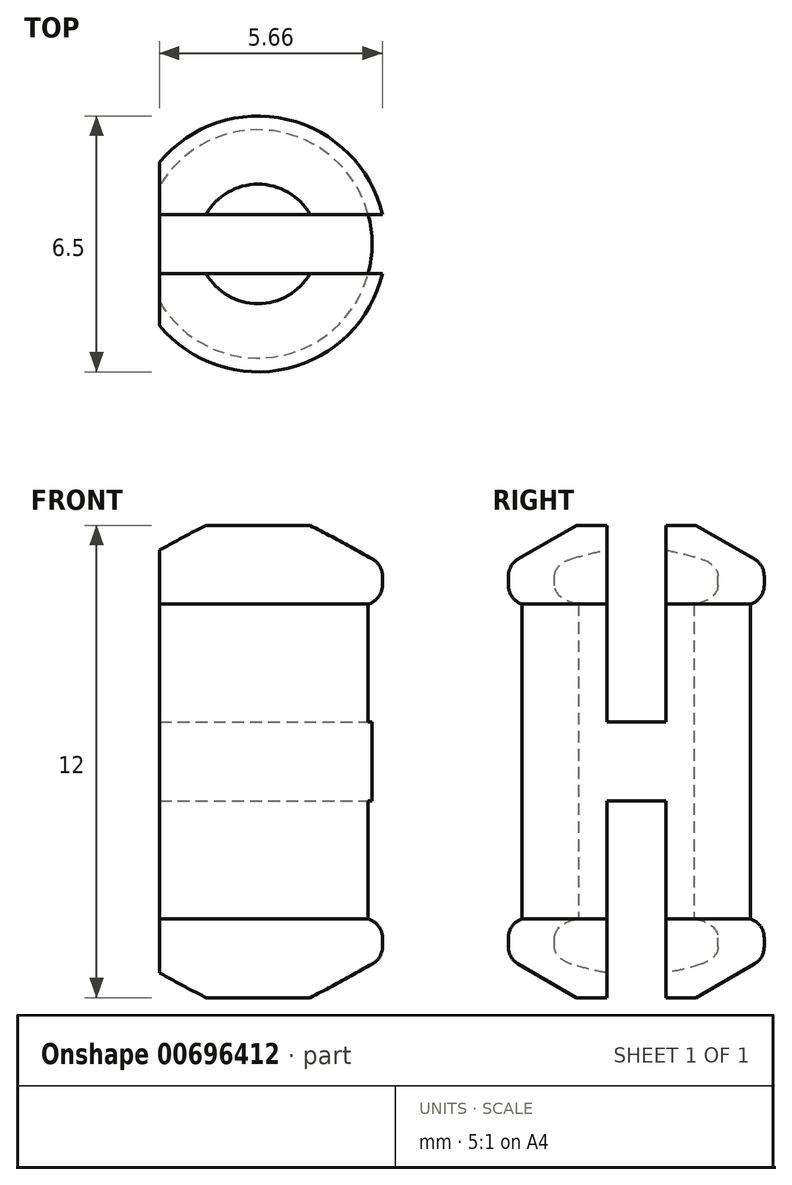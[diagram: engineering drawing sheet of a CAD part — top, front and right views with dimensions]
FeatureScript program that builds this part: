
annotation { "Feature Type Name" : "Feature", "Feature Type Description" : "" }
export const myFeature = defineFeature(function(context is Context, id is Id, definition is map)
    precondition{}
    {
        {
            var Q0;
            Q0=qCreatedBy(makeId("Top.planeOp"),FACE);
            var sketch = newSketch(context, id + "F0", { "sketchPlane" : qUnion([Q0])});
            skCircle(sketch, "E0", {"center": v(0, 0) * mm, "radius": 3.25 * mm});
            skSolve(sketch);
        }
        {
            var Q0;
            Q0=qSketchRegion(id+"F0",true);
            extrude(context, id + "F1", {"entities" : qUnion([Q0]), "depth" : 2 * mm, "offsetDistance" : 25 * mm});
        }
        {
            var Q0;
            Q0=makeQuery(id+"F1.opExtrude","CAP_FACE",FACE,{"disambiguationData":[OSD([sQuery(id+"F0.wireOp",EDGE,"E0")])],"isStart":false});
            var sketch = newSketch(context, id + "F2", { "sketchPlane" : qUnion([Q0])});
            skCircle(sketch, "E1", {"center": v(0, 0) * mm, "radius": 2.9 * mm});
            skSolve(sketch);
        }
        {
            var Q0;
            Q0=qSketchRegion(id+"F2",true);
            extrude(context, id + "F3", {"entities" : qUnion([Q0]), "operationType" : NewBodyOperationType.ADD, "depth" : 8 * mm, "offsetDistance" : 25 * mm});
        }
        {
            var Q0;
            Q0=makeQuery(id+"F3.opExtrude","CAP_FACE",FACE,{"disambiguationData":[OSD([sQuery(id+"F2.wireOp",EDGE,"E1")])],"isStart":false});
            var sketch = newSketch(context, id + "F4", { "sketchPlane" : qUnion([Q0])});
            skCircle(sketch, "E2", {"center": v(0, 0) * mm, "radius": 3.25 * mm});
            skSolve(sketch);
        }
        {
            var Q0;
            Q0=qSketchRegion(id+"F4",true);
            extrude(context, id + "F5", {"entities" : qUnion([Q0]), "operationType" : NewBodyOperationType.ADD, "depth" : 2 * mm, "offsetDistance" : 25 * mm});
        }
        {
            var Q0;
            Q0=makeQuery(id+"F1.opExtrude","CAP_EDGE",EDGE,{"disambiguationData":[OSD([sQuery(id+"F0.wireOp",EDGE,"E0")])],"isStart":false});
            var Q1;
            Q1=makeQuery(id+"F5.opExtrude","CAP_EDGE",EDGE,{"disambiguationData":[OSD([sQuery(id+"F4.wireOp",EDGE,"E2")])],"isStart":true});
            fillet(context, id + "F6", {"entities" : qUnion([Q0, Q1]), "radius" : 0.5 * mm, "tangentPropagation" : true, "allowEdgeOverflow" : false});
        }
        {
            var Q0;
            Q0=makeQuery(id+"F1.opExtrude","CAP_FACE",FACE,{"disambiguationData":[OSD([sQuery(id+"F0.wireOp",EDGE,"E0")])],"isStart":true});
            var sketch = newSketch(context, id + "F7", { "sketchPlane" : qUnion([Q0])});
            skLineSegment(sketch, "E3", {"start": v(-3.16, -0.75) * mm, "end": v(3.16, -0.75) * mm});
            skLineSegment(sketch, "E4", {"start": v(3.16, 0.75) * mm, "end": v(-3.16, 0.75) * mm});
            skArc(sketch, "E5", {"start": v(-3.16, 0.75) * mm, "mid": v(-3.25, 0) * mm, "end": v(-3.16, -0.75) * mm});
            skArc(sketch, "E6", {"start": v(3.16, -0.75) * mm, "mid": v(3.25, 0) * mm, "end": v(3.16, 0.75) * mm});
            skSolve(sketch);
        }
        {
            var Q0;
            Q0=qSketchRegion(id+"F7",true);
            extrude(context, id + "F8", {"entities" : qUnion([Q0]), "operationType" : NewBodyOperationType.REMOVE, "oppositeDirection" : true, "depth" : 5 * mm, "offsetDistance" : 25 * mm});
        }
        {
            var Q0;
            Q0=makeQuery(id+"F5.opExtrude","CAP_FACE",FACE,{"disambiguationData":[OSD([sQuery(id+"F4.wireOp",EDGE,"E2")])],"isStart":false});
            var sketch = newSketch(context, id + "F9", { "sketchPlane" : qUnion([Q0])});
            skLineSegment(sketch, "E7", {"start": v(-3.16, -0.75) * mm, "end": v(3.16, -0.75) * mm});
            skLineSegment(sketch, "E8", {"start": v(3.16, 0.75) * mm, "end": v(-3.16, 0.75) * mm});
            skArc(sketch, "E9", {"start": v(3.16, -0.75) * mm, "mid": v(3.25, 0) * mm, "end": v(3.16, 0.75) * mm});
            skArc(sketch, "E10", {"start": v(-3.16, 0.75) * mm, "mid": v(-3.25, 0) * mm, "end": v(-3.16, -0.75) * mm});
            skSolve(sketch);
        }
        {
            var Q0;
            Q0=qSketchRegion(id+"F9",true);
            extrude(context, id + "F10", {"entities" : qUnion([Q0]), "operationType" : NewBodyOperationType.REMOVE, "oppositeDirection" : true, "depth" : 5 * mm, "offsetDistance" : 25 * mm});
        }
        {
            var Q0;
            {var subQ0=sQuery(id+"F0.wireOp",EDGE,"E0");Q0=makeQuery(id+"F8.boolean.opBoolean","SPLIT",EDGE,{"disambiguationData":[TD([makeQuery(id+"F8.opExtrude","SWEPT_FACE",FACE,{"disambiguationData":[OSD([sQuery(id+"F7.wireOp",EDGE,"E3")])]})])],"derivedFrom":makeQuery(id+"F1.opExtrude","CAP_EDGE",EDGE,{"disambiguationData":[OSD([subQ0])],"isStart":true})});}
            var Q1;
            {var subQ0=sQuery(id+"F0.wireOp",EDGE,"E0");Q1=makeQuery(id+"F8.boolean.opBoolean","SPLIT",EDGE,{"disambiguationData":[TD([makeQuery(id+"F8.opExtrude","SWEPT_FACE",FACE,{"disambiguationData":[OSD([sQuery(id+"F7.wireOp",EDGE,"E4")])]})])],"derivedFrom":makeQuery(id+"F1.opExtrude","CAP_EDGE",EDGE,{"disambiguationData":[OSD([subQ0])],"isStart":true})});}
            chamfer(context, id + "F11", {"entities" : qUnion([Q0, Q1]), "chamferType" : ChamferType.OFFSET_ANGLE, "width" : 1 * mm, "oppositeDirection" : false, "angle" : 60 * degree, "tangentPropagation" : true});
        }
        {
            var Q0;
            {var subQ0=sQuery(id+"F4.wireOp",EDGE,"E2");Q0=makeQuery(id+"F10.boolean.opBoolean","SPLIT",EDGE,{"disambiguationData":[TD([makeQuery(id+"F10.opExtrude","SWEPT_FACE",FACE,{"disambiguationData":[OSD([sQuery(id+"F9.wireOp",EDGE,"E7")])]})])],"derivedFrom":makeQuery(id+"F5.opExtrude","CAP_EDGE",EDGE,{"disambiguationData":[OSD([subQ0])],"isStart":false})});}
            var Q1;
            {var subQ0=sQuery(id+"F4.wireOp",EDGE,"E2");Q1=makeQuery(id+"F10.boolean.opBoolean","SPLIT",EDGE,{"disambiguationData":[TD([makeQuery(id+"F10.opExtrude","SWEPT_FACE",FACE,{"disambiguationData":[OSD([sQuery(id+"F9.wireOp",EDGE,"E8")])]})])],"derivedFrom":makeQuery(id+"F5.opExtrude","CAP_EDGE",EDGE,{"disambiguationData":[OSD([subQ0])],"isStart":false})});}
            chamfer(context, id + "F12", {"entities" : qUnion([Q0, Q1]), "chamferType" : ChamferType.OFFSET_ANGLE, "width" : 1 * mm, "oppositeDirection" : true, "angle" : 60 * degree, "tangentPropagation" : true});
        }
        {
            var Q0;
            {var subQ0=sQuery(id+"F4.wireOp",EDGE,"E2");var subQ2=makeQuery(id+"F10.opExtrude","SWEPT_FACE",FACE,{"disambiguationData":[OSD([sQuery(id+"F9.wireOp",EDGE,"E7")])]});var subQ3=makeQuery(id+"F5.opExtrude","SWEPT_FACE",FACE,{"disambiguationData":[OSD([subQ0])]});Q0=makeQuery(id+"F12.opChamfer","BLEND_EDGE",EDGE,{"blendedFrom":[makeQuery(id+"F10.boolean.opBoolean","SPLIT",EDGE,{"disambiguationData":[TD([subQ2])],"derivedFrom":makeQuery(id+"F5.opExtrude","CAP_EDGE",EDGE,{"disambiguationData":[OSD([subQ0])],"isStart":false})}),makeQuery(id+"F10.boolean.opBoolean","SPLIT",FACE,{"disambiguationData":[TD([subQ2])],"derivedFrom":subQ3})],"blendedInto":[makeQuery(id+"F10.boolean.opBoolean","SPLIT",FACE,{"disambiguationData":[TD([subQ2])],"derivedFrom":subQ3})]});}
            var Q1;
            {var subQ0=sQuery(id+"F4.wireOp",EDGE,"E2");var subQ2=makeQuery(id+"F10.opExtrude","SWEPT_FACE",FACE,{"disambiguationData":[OSD([sQuery(id+"F9.wireOp",EDGE,"E8")])]});var subQ3=makeQuery(id+"F5.opExtrude","SWEPT_FACE",FACE,{"disambiguationData":[OSD([subQ0])]});Q1=makeQuery(id+"F12.opChamfer","BLEND_EDGE",EDGE,{"blendedFrom":[makeQuery(id+"F10.boolean.opBoolean","SPLIT",EDGE,{"disambiguationData":[TD([subQ2])],"derivedFrom":makeQuery(id+"F5.opExtrude","CAP_EDGE",EDGE,{"disambiguationData":[OSD([subQ0])],"isStart":false})}),makeQuery(id+"F10.boolean.opBoolean","SPLIT",FACE,{"disambiguationData":[TD([subQ2])],"derivedFrom":subQ3})],"blendedInto":[makeQuery(id+"F10.boolean.opBoolean","SPLIT",FACE,{"disambiguationData":[TD([subQ2])],"derivedFrom":subQ3})]});}
            var Q2;
            {var subQ0=sQuery(id+"F0.wireOp",EDGE,"E0");var subQ2=makeQuery(id+"F8.opExtrude","SWEPT_FACE",FACE,{"disambiguationData":[OSD([sQuery(id+"F7.wireOp",EDGE,"E4")])]});var subQ3=makeQuery(id+"F1.opExtrude","SWEPT_FACE",FACE,{"disambiguationData":[OSD([subQ0])]});Q2=makeQuery(id+"F11.opChamfer","BLEND_EDGE",EDGE,{"blendedFrom":[makeQuery(id+"F8.boolean.opBoolean","SPLIT",EDGE,{"disambiguationData":[TD([subQ2])],"derivedFrom":makeQuery(id+"F1.opExtrude","CAP_EDGE",EDGE,{"disambiguationData":[OSD([subQ0])],"isStart":true})}),makeQuery(id+"F8.boolean.opBoolean","SPLIT",FACE,{"disambiguationData":[TD([subQ2])],"derivedFrom":subQ3})],"blendedInto":[makeQuery(id+"F8.boolean.opBoolean","SPLIT",FACE,{"disambiguationData":[TD([subQ2])],"derivedFrom":subQ3})]});}
            var Q3;
            {var subQ0=sQuery(id+"F0.wireOp",EDGE,"E0");var subQ2=makeQuery(id+"F8.opExtrude","SWEPT_FACE",FACE,{"disambiguationData":[OSD([sQuery(id+"F7.wireOp",EDGE,"E3")])]});var subQ3=makeQuery(id+"F1.opExtrude","SWEPT_FACE",FACE,{"disambiguationData":[OSD([subQ0])]});Q3=makeQuery(id+"F11.opChamfer","BLEND_EDGE",EDGE,{"blendedFrom":[makeQuery(id+"F8.boolean.opBoolean","SPLIT",EDGE,{"disambiguationData":[TD([subQ2])],"derivedFrom":makeQuery(id+"F1.opExtrude","CAP_EDGE",EDGE,{"disambiguationData":[OSD([subQ0])],"isStart":true})}),makeQuery(id+"F8.boolean.opBoolean","SPLIT",FACE,{"disambiguationData":[TD([subQ2])],"derivedFrom":subQ3})],"blendedInto":[makeQuery(id+"F8.boolean.opBoolean","SPLIT",FACE,{"disambiguationData":[TD([subQ2])],"derivedFrom":subQ3})]});}
            fillet(context, id + "F13", {"entities" : qUnion([Q0, Q1, Q2, Q3]), "radius" : 0.5 * mm, "tangentPropagation" : true, "allowEdgeOverflow" : false});
        }
        {
            var Q0;
            {var subQ0=sQuery(id+"F4.wireOp",EDGE,"E2");Q0=makeQuery(id+"F10.boolean.opBoolean","SPLIT",FACE,{"disambiguationData":[TD([makeQuery(id+"F10.opExtrude","SWEPT_FACE",FACE,{"disambiguationData":[OSD([sQuery(id+"F9.wireOp",EDGE,"E8")])]})])],"derivedFrom":makeQuery(id+"F5.opExtrude","CAP_FACE",FACE,{"disambiguationData":[OSD([subQ0])],"isStart":false})});}
            var sketch = newSketch(context, id + "F14", { "sketchPlane" : qUnion([Q0])});
            skArc(sketch, "E11", {"start": v(-2.5, 2.08) * mm, "mid": v(-3.25, 0) * mm, "end": v(-2.5, -2.08) * mm});
            skLineSegment(sketch, "E12", {"start": v(-2.5, -2.08) * mm, "end": v(-2.5, 2.08) * mm});
            skSolve(sketch);
        }
        {
            var Q0;
            Q0=qSketchRegion(id+"F14",true);
            extrude(context, id + "F15", {"entities" : qUnion([Q0]), "operationType" : NewBodyOperationType.REMOVE, "oppositeDirection" : true, "depth" : 25 * mm, "offsetDistance" : 25 * mm});
        }
    });
